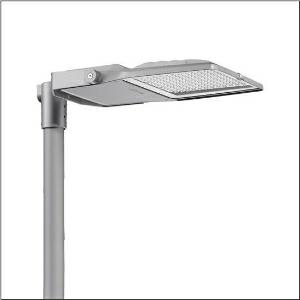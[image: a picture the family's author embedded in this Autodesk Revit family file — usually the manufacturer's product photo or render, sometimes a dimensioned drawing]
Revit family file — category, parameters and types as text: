
# Revit family: floodlight_fl_21_iq_midi___pl43_5xa7781e4a3a_24f4
name_source: partatom
category: Lighting Fixtures
units: mm (PartAtom-declared; Revit-internal decimal feet)

## family parameters
Cut with Voids When Loaded = No
Host = Face
Light Source = No
Part Type = Normal
Room Calculation Point = No
Round Connector Dimension = Use Diameter
Shared = No

## types (1)
- --- (1 x LED, 28730 lm, 208.1 W, 4000K)
    Apparent Load = 208 VA
    CIE Flux Codes = 27 78 99 100 100
    Color Rendering = 70
    Color Temperature = 4000K
    Default Elevation = 1800 mm
    Description = Floodlight FL 21 iQ midi, floodlight, primary light control with lens, of PMMA, primary optical cover: protective disc, of toughened safety glass, transparent, light distribution: PL43, light emission: direct distribution, installation type: surface-mounted, LED, High Power LED, rated luminous flux: 28.730lm, luminous efficacy: 138lm/W, light colour: 740, colour temperature: 4000K, control gear: iQ Comfort/DALI, control: optimised constant luminous flux control (CLO 2.0), Desk-Remote (wireless, voltage-free reading and setting of iQ features in the workshop via application-optimized NFC function/RFID function), Light-Fading, Smart-Wire, Night-Set, Lumen-Switch, Temp-Guard, Auto-Match, with terminal, 6-pole, mains connection: 220..240V, AC, 50/60Hz, start of lifetime: 208W, end of service life: 227W, reduction: 90W, luminaire housing, of diecast aluminium, powder-coated, Siteco® metallic grey (DB 702S), corrosivity category C5 mid according to DIN EN ISO 12944, suitable for swimming pools, chlorine-resistant, sealing non-destructively replaceable, please order mast flange separately, mast bracket, of steel, galvanised, powder-coated, Siteco® metallic grey (DB 702S), protection rating (complete): IP66, insulation class (complete): insulation class II (safety insulation), certification: CE, ENEC, VDE, protection symbol: D, impact resistance: IK08, permissible operating ambient temperature: -40..+40°C, permissible operating ambient temperature for outdoor applications: -40..+50°C, standard: DIN EN 12944, LABS conformity tested according to VDMA 24364:2018-05, packaging unit: 1 piece

Light Distribution: PL43
    Height = 76 mm
    Lamp = 1 x LED
    Lamp Light Flux = 28730 lm
    Lamp Power = 208.1 W
    Lamp count = 1
    Length = 657 mm
    Luminous efficacy = 138 lm/W
    Manufacturer = Siteco
    ModVariant = No
    Model = 5XA7781E4A3A
    Number of Poles = 1
    OnlyDefault = Yes
    Power Factor = 1
    Product Name = Floodlight FL 21 iQ midi | PL43
    Product group = floodlight | pylon annexe
    ProductGroupID = 6200
    Protection Class = Protection class II
    Protection Degree = IP 66
    RLX_Detail_Level = 1
    RLX_Emergency_Light_Flux = 0 lm
    RLX_Emergency_Type = 0
    RLX_Emergency_Type_DB = No
    RlxData = <blob elided: 153309 chars, md5=c1818532>
    Socket = socket
    Standby Power = 0 W
    System Light Flux = 28730 lm
    System Power = 208 W
    Type Comments = factory setting: luminous flux: 100 % | dim-lin: 254 | 710 mA
    Type Image = l_1007123.jpg
    URL = http://relux.com
    VarID = @adj_105300
    Voltage = 0 V
    Weight = 0.00 kg
    Width = 442 mm

## geometry (parser evidence)
native form markers: Blend x4, Sweep x11
no freeform markers — native parametric forms only
